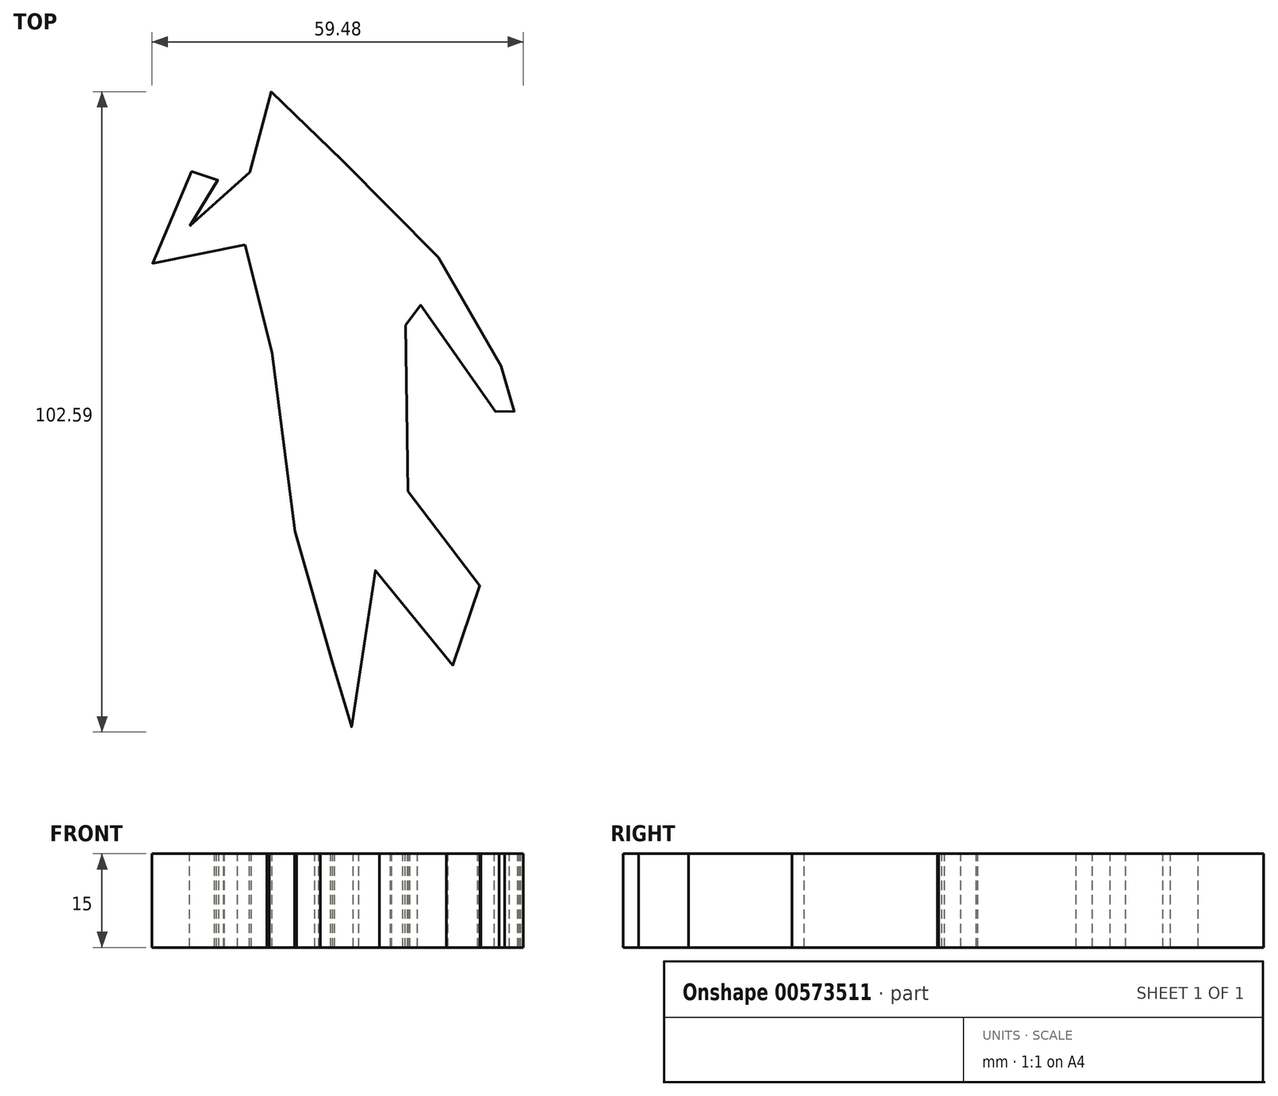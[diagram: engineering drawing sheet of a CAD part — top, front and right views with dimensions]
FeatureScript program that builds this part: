
annotation { "Feature Type Name" : "Feature", "Feature Type Description" : "" }
export const myFeature = defineFeature(function(context is Context, id is Id, definition is map)
    precondition{}
    {
        {
            var Q0;
            Q0=qCreatedBy(makeId("Top.planeOp"),FACE);
            var sketch = newSketch(context, id + "F0", { "sketchPlane" : qUnion([Q0])});
            skPoint(sketch, "E0.211.internal.snap0", {"position": v(1.05, 56.44) * mm});
            skPoint(sketch, "E0.216.internal.snap0", {"position": v(1.05, 56.44) * mm});
            skFitSpline(sketch, "E0", {"points": [v(-13.26, 26.56) * mm, v(-14.74, 25.82) * mm, v(-16.9, 24.62) * mm, v(-19.4, 23.03) * mm, v(-21.4, 21.9) * mm, v(-23.17, 21.32) * mm, v(-25.22, 21.15) * mm, v(-26.87, 21.15) * mm, v(-27.5, 21.66) * mm, v(-28, 23.03) * mm, v(-28.12, 24.68) * mm, v(-28.12, 26.5) * mm, v(-27.2, 28.84) * mm, v(-26.1, 31.57) * mm, v(-25.4, 32.97) * mm, v(-24.83, 33.93) * mm, v(-24.06, 34.5) * mm, v(-23.82, 34.78) * mm, v(-23.57, 35.33) * mm, v(-22.21, 38) * mm, v(-21.98, 38.29) * mm, v(-21.5, 38.45) * mm, v(-19.68, 39.74) * mm, v(-18.6, 40.25) * mm, v(-17.85, 40.49) * mm, v(-17.14, 40.67) * mm, v(-16.72, 40.67) * mm, v(-16.57, 40.46) * mm, v(-16.69, 40.13) * mm, v(-17.05, 39.92) * mm, v(-17.61, 39.71) * mm, v(-17.85, 39.68) * mm, v(-17.64, 39.47) * mm, v(-17.5, 39.17) * mm, v(-17.8, 38.4) * mm, v(-18.15, 37.83) * mm, v(-18, 37.56) * mm, v(-17.7, 37.05) * mm, v(-17.26, 36.48) * mm, v(-16.99, 35.86) * mm, v(-16.78, 35.47) * mm, v(-16.78, 35.14) * mm, v(-17.17, 35.05) * mm, v(-17.64, 35.05) * mm, v(-18.24, 35.5) * mm, v(-18.99, 36.07) * mm, v(-19.29, 36.19) * mm, v(-19.77, 34.78) * mm, v(-20.7, 33.59) * mm, v(-21.29, 33) * mm, v(-21.53, 32.45) * mm, v(-21.68, 31.86) * mm, v(-22.15, 29.32) * mm, v(-22.15, 29.08) * mm, v(-21.95, 29.17) * mm, v(-21.83, 29.67) * mm, v(-20.9, 30.63) * mm, v(-18.99, 32.4) * mm, v(-17.38, 34.1) * mm, v(-15.88, 35.4) * mm, v(-14.9, 35.95) * mm, v(-14.33, 36.42) * mm, v(-13.07, 36.96) * mm, v(-12.3, 37.3) * mm, v(-12.48, 38.07) * mm, v(-12.6, 39) * mm, v(-12.72, 40.28) * mm, v(-13.07, 40.52) * mm, v(-13.58, 41.17) * mm, v(-14.31, 43.97) * mm, v(-14.48, 45.5) * mm, v(-14, 47.68) * mm, v(-12.94, 49.13) * mm, v(-11.85, 49.98) * mm, v(-10.46, 50.6) * mm, v(-8.62, 51.12) * mm, v(-6.2, 50.42) * mm, v(-4.1, 49.08) * mm, v(-2.77, 46.73) * mm, v(-1.57, 44.83) * mm, v(-1.57, 43.68) * mm, v(-1.82, 42.54) * mm, v(-2.07, 41.71) * mm, v(-1.12, 41.02) * mm, v(2.18, 40.13) * mm, v(3.64, 39.87) * mm, v(6.82, 38.73) * mm, v(9.68, 36.57) * mm, v(13.05, 32.57) * mm, v(15.57, 27.34) * mm, v(15.94, 26.16) * mm, v(16.68, 25.72) * mm, v(17.86, 24.24) * mm, v(18.6, 22.7) * mm, v(18.74, 22.33) * mm, v(19.33, 21.74) * mm, v(20.44, 19.82) * mm, v(21.54, 18.06) * mm, v(22.85, 15.86) * mm, v(24.89, 12.1) * mm, v(27.46, 7.9) * mm, v(27.78, 7.17) * mm, v(28.02, 6.92) * mm, v(29.76, 5.4) * mm, v(30.03, 5.1) * mm, v(30.5, 4.33) * mm, v(30.92, 3.14) * mm, v(30.86, 2.74) * mm, v(30.68, 2.31) * mm, v(30.64, 1.86) * mm, v(30.4, 1.06) * mm, v(30.77, 0.36) * mm, v(31.29, -0.37) * mm, v(31.16, -0.9) * mm, v(30.8, -0.9) * mm, v(30.34, -0.43) * mm, v(29.94, 0) * mm, v(29.58, -0.62) * mm, v(29.03, -1.01) * mm, v(28.45, -1.04) * mm, v(28.36, -0.68) * mm, v(28.72, 0) * mm, v(29.09, 0.82) * mm, v(28.75, 1.12) * mm, v(27.93, 2) * mm, v(27.1, 2.44) * mm, v(26.7, 2.59) * mm, v(26.83, 1.98) * mm, v(27.2, 1.4) * mm, v(27.4, 0.91) * mm, v(27.44, 0.27) * mm, v(27.29, -0.37) * mm, v(26.98, -0.25) * mm, v(26.25, 1) * mm, v(25.4, 2.22) * mm, v(24.48, 3.63) * mm, v(24.14, 5.15) * mm, v(24.11, 5.37) * mm, v(23.84, 5.21) * mm, v(23.5, 5.1) * mm, v(23.23, 5.12) * mm, v(23.04, 5.37) * mm, v(19.5, 11.04) * mm, v(14.67, 17.21) * mm, v(10.7, 23.22) * mm, v(10.02, 23.73) * mm, v(10.1, 23.22) * mm, v(10.18, 21.36) * mm, v(10.27, 20.34) * mm, v(10.86, 19.41) * mm, v(11.62, 17.38) * mm, v(12.72, 15.69) * mm, v(12.47, 14.67) * mm, v(12.47, 13.57) * mm, v(13.65, 10.7) * mm, v(14.16, 3) * mm, v(14.25, -2.25) * mm, v(12.98, -9.7) * mm, v(12.98, -10.62) * mm, v(13.15, -12.32) * mm, v(12.8, -12.9) * mm, v(12.05, -16.97) * mm, v(13.11, -17.8) * mm, v(14.57, -19.18) * mm, v(17.58, -21.86) * mm, v(19.45, -24.38) * mm, v(20.01, -24.46) * mm, v(21.8, -26) * mm, v(24.16, -27.7) * mm, v(24.43, -28.9) * mm, v(24.43, -30.74) * mm, v(24.09, -30.93) * mm, v(24.09, -31.94) * mm, v(24.29, -34.95) * mm, v(24.34, -36) * mm, v(23.9, -37.24) * mm, v(22.8, -38.88) * mm, v(21.7, -40.37) * mm, v(21, -40.87) * mm, v(20.36, -40.97) * mm, v(19.97, -40.72) * mm, v(19.57, -40.07) * mm, v(19.27, -38.53) * mm, v(19.02, -36.9) * mm, v(19.02, -36.05) * mm, v(19.22, -35.45) * mm, v(18.03, -34.5) * mm, v(14.5, -31.72) * mm, v(11.32, -29.09) * mm, v(7.34, -25.3) * mm, v(6.3, -24.02) * mm, v(5.65, -23.62) * mm, v(5, -23.52) * mm, v(4.96, -23.02) * mm, v(4.6, -22.43) * mm, v(4.4, -23.02) * mm, v(4.06, -23.62) * mm, v(4.3, -24.41) * mm, v(4.76, -25.96) * mm, v(5.35, -28.69) * mm, v(6.15, -33.7) * mm, v(6.74, -37.83) * mm, v(7, -41.86) * mm, v(7.9, -44.86) * mm, v(8.15, -47) * mm, v(8.05, -48.85) * mm, v(6.78, -48.92) * mm, v(5.44, -49.1) * mm, v(4.36, -49.68) * mm, v(3.72, -50.7) * mm, v(2.9, -50.95) * mm, v(1.05, -51.33) * mm, v(0, -51.46) * mm, v(-1.17, -51.02) * mm, v(-0.98, -49.94) * mm, v(0, -48.66) * mm, v(1.05, -47.58) * mm, v(0.54, -45.3) * mm, v(0.54, -43.58) * mm, v(0.74, -40.5) * mm, v(0.43, -39.52) * mm, v(-0.24, -37.8) * mm, v(-1.16, -34.98) * mm, v(-2.57, -30.6) * mm, v(-3.93, -26.8) * mm, v(-5.15, -22.79) * mm, v(-5.36, -21.36) * mm, v(-5.22, -18.99) * mm, v(-5.02, -17.83) * mm, v(-5.9, -14.78) * mm, v(-7.46, -9.83) * mm, v(-8.82, -3.04) * mm, v(-9.39, 4.63) * mm, v(-9.02, 9.84) * mm, v(-9.57, 11.05) * mm, v(-9.76, 11.7) * mm, v(-9.39, 12.91) * mm, v(-9.39, 15.8) * mm, v(-9.85, 18.59) * mm, v(-10.23, 20.63) * mm, v(-11.43, 22.58) * mm, v(-12.09, 24.72) * mm, v(-13.26, 26.56) * mm]});
            skSolve(sketch);
        }
        {
            var Q0;
            Q0=sQuery(id+"F0.wireOp",EDGE,"E0");
            extrude(context, id + "F1", {"bodyType" : ToolBodyType.SURFACE, "surfaceEntities" : qUnion([Q0]), "depth" : 15 * mm, "offsetDistance" : 25.4 * mm});
        }
    });
